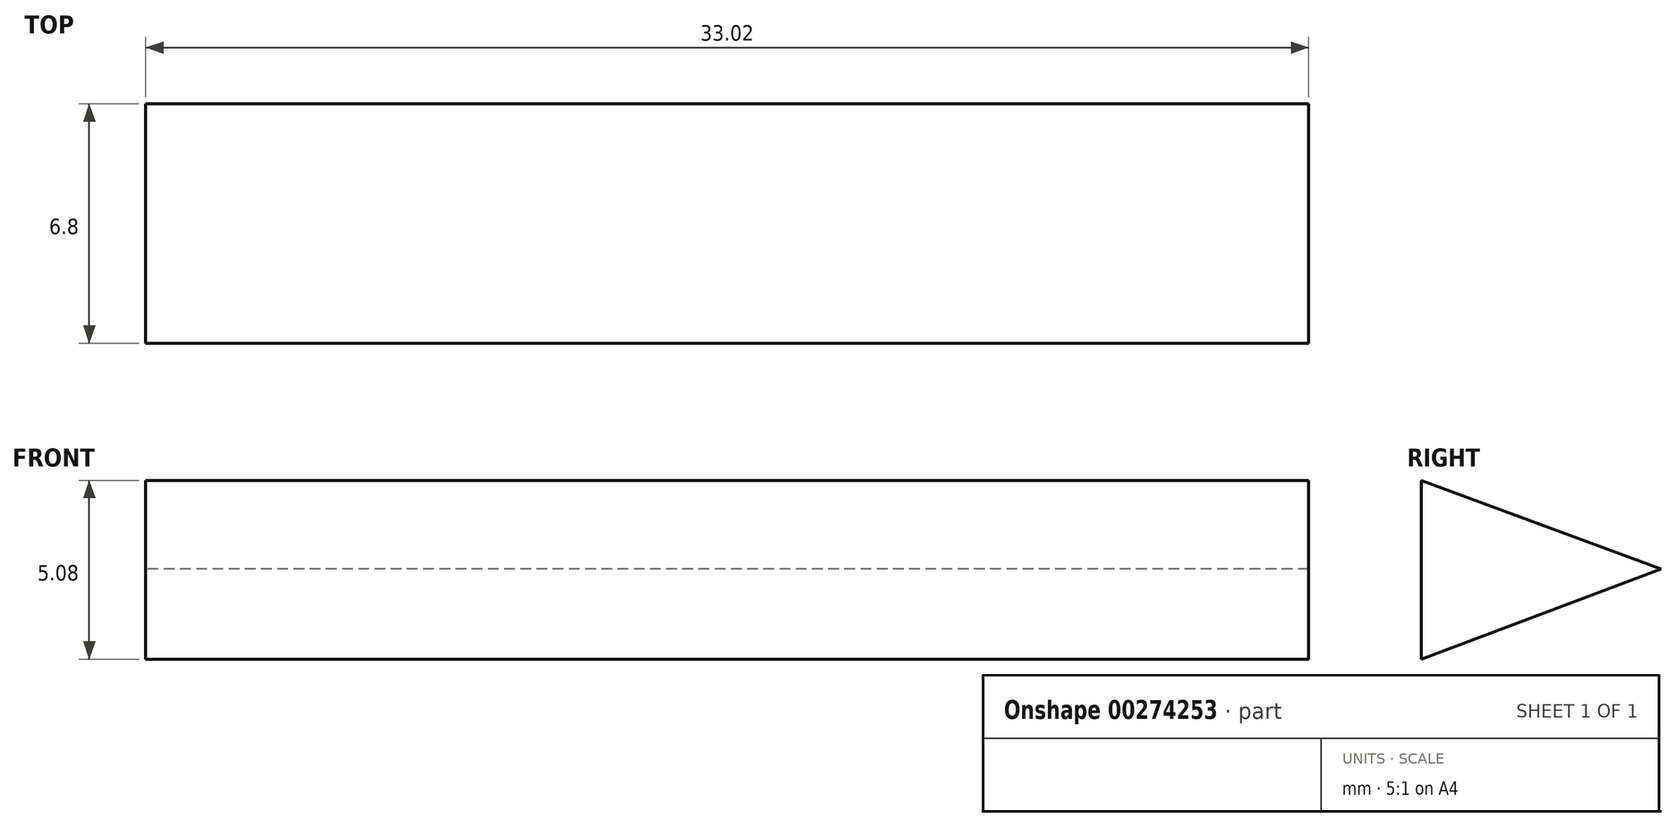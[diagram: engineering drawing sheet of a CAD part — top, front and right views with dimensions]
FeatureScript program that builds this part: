
annotation { "Feature Type Name" : "Feature", "Feature Type Description" : "" }
export const myFeature = defineFeature(function(context is Context, id is Id, definition is map)
    precondition{}
    {
        {
            var Q0;
            Q0=qCreatedBy(makeId("Front.planeOp"),FACE);
            var sketch = newSketch(context, id + "F0", { "sketchPlane" : qUnion([Q0])});
            skCircle(sketch, "E0", {"center": v(0, 0) * mm, "radius": 2.42 * mm});
            skSolve(sketch);
        }
        {
            var Q0;
            Q0=sQuery(id+"F0.wireOp",EDGE,"E0");
            extrude(context, id + "F1", {"bodyType" : ToolBodyType.SURFACE, "surfaceEntities" : qUnion([Q0]), "depth" : 58.42 * mm});
        }
        {
            var Q0;
            Q0=qCreatedBy(makeId("Right.planeOp"),FACE);
            var sketch = newSketch(context, id + "F2", { "sketchPlane" : qUnion([Q0])});
            skLineSegment(sketch, "E1", {"start": v(0, 2.52) * mm, "end": v(0, -2.56) * mm});
            skLineSegment(sketch, "E2", {"start": v(0, -2.56) * mm, "end": v(6.8, 0) * mm});
            skLineSegment(sketch, "E3", {"start": v(6.8, 0) * mm, "end": v(0, 2.52) * mm});
            skSolve(sketch);
        }
        {
            var Q0;
            Q0 = qSketchRegion(id + "F2", true);
            extrude(context, id + "F3", {"entities" : qUnion([Q0]), "endBound" : BoundingType.SYMMETRIC, "depth" : 33.02 * mm});
        }
    });
